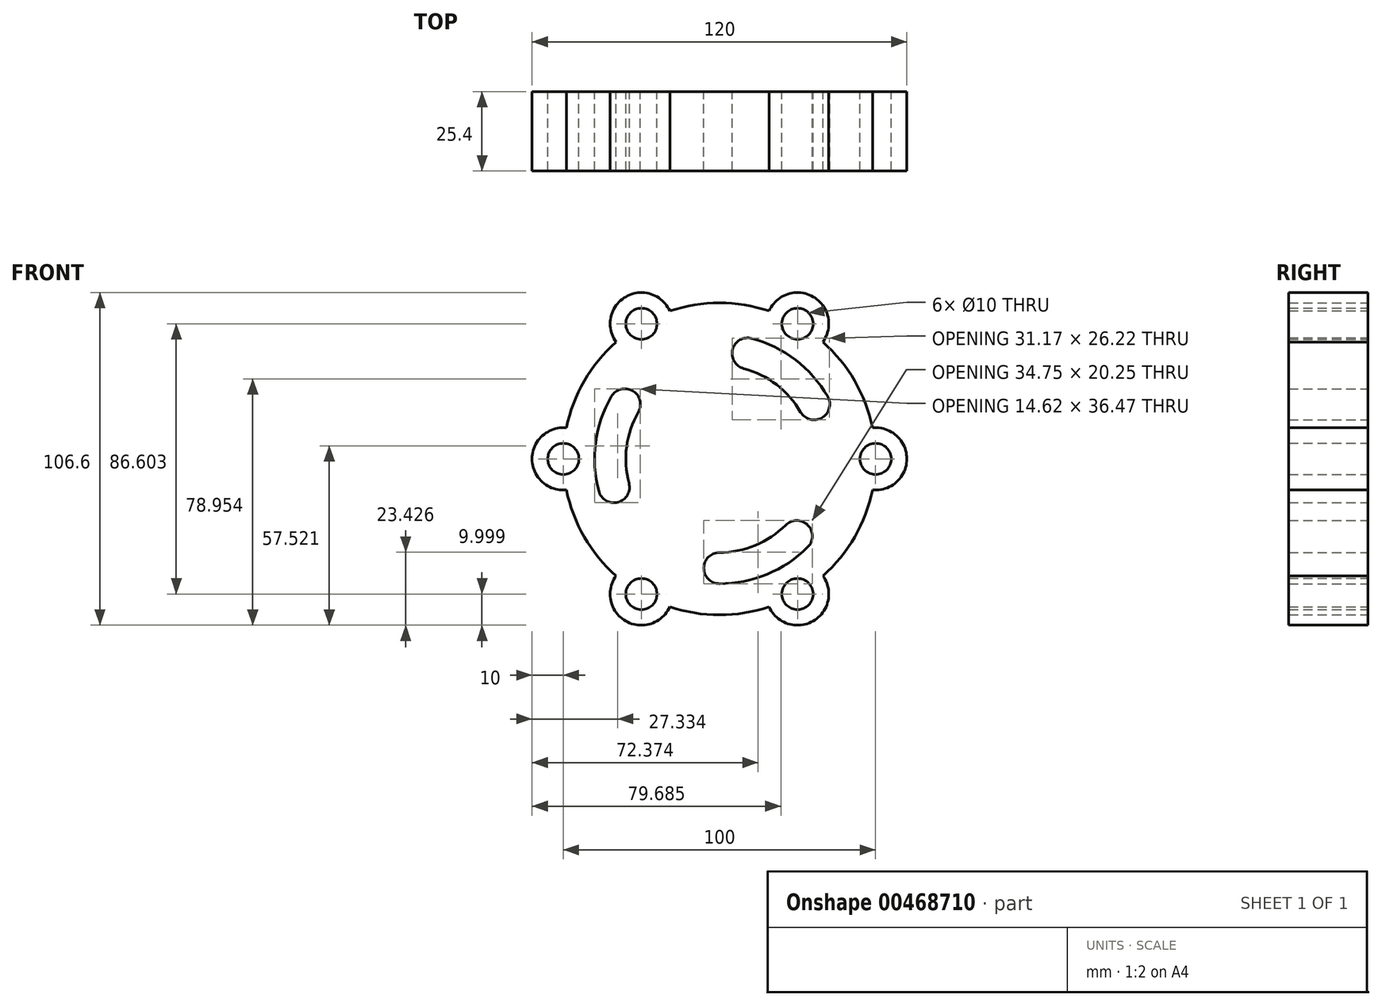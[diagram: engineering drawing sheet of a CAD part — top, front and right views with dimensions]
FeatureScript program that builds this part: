
annotation { "Feature Type Name" : "Feature", "Feature Type Description" : "" }
export const myFeature = defineFeature(function(context is Context, id is Id, definition is map)
    precondition{}
    {
        {
            var Q0;
            Q0=qCreatedBy(makeId("Front.planeOp"),FACE);
            var sketch = newSketch(context, id + "F0", { "sketchPlane" : qUnion([Q0])});
            skArc(sketch, "E0", {"start": v(-49, -9.95) * mm, "mid": v(-43.3, -25) * mm, "end": v(-33.12, -37.46) * mm});
            skArc(sketch, "E1", {"start": v(49, -9.95) * mm, "mid": v(60, 0) * mm, "end": v(49, 9.95) * mm});
            skCircle(sketch, "E2", {"center": v(50, 0) * mm, "radius": 5 * mm});
            skArc(sketch, "E3.1.0", {"start": v(33.12, 37.46) * mm, "mid": v(30, 51.96) * mm, "end": v(15.88, 47.41) * mm});
            skCircle(sketch, "E3.1.1", {"center": v(25, 43.3) * mm, "radius": 5 * mm});
            skArc(sketch, "E3.2.0", {"start": v(-15.88, 47.41) * mm, "mid": v(-30, 51.96) * mm, "end": v(-33.12, 37.46) * mm});
            skCircle(sketch, "E3.2.1", {"center": v(-25, 43.3) * mm, "radius": 5 * mm});
            skArc(sketch, "E3.3.0", {"start": v(-49, 9.95) * mm, "mid": v(-60, 0) * mm, "end": v(-49, -9.95) * mm});
            skCircle(sketch, "E3.3.1", {"center": v(-50, 0) * mm, "radius": 5 * mm});
            skArc(sketch, "E3.4.0", {"start": v(-33.12, -37.46) * mm, "mid": v(-30, -51.96) * mm, "end": v(-15.88, -47.41) * mm});
            skCircle(sketch, "E3.4.1", {"center": v(-25, -43.3) * mm, "radius": 5 * mm});
            skArc(sketch, "E3.5.0", {"start": v(15.88, -47.41) * mm, "mid": v(30, -51.96) * mm, "end": v(33.12, -37.46) * mm});
            skCircle(sketch, "E3.5.1", {"center": v(25, -43.3) * mm, "radius": 5 * mm});
            skArc(sketch, "E4.trimOffspring", {"start": v(-33.12, 37.46) * mm, "mid": v(-43.3, 25) * mm, "end": v(-49, 9.95) * mm});
            skArc(sketch, "E5.trimOffspring", {"start": v(-15.88, -47.41) * mm, "mid": v(0, -50) * mm, "end": v(15.88, -47.41) * mm});
            skArc(sketch, "E6.trimOffspring", {"start": v(33.12, -37.46) * mm, "mid": v(43.3, -25) * mm, "end": v(49, -9.95) * mm});
            skArc(sketch, "E7.trimOffspring", {"start": v(49, 9.95) * mm, "mid": v(43.3, 25) * mm, "end": v(33.12, 37.46) * mm});
            skArc(sketch, "E8.trimOffspring", {"start": v(15.88, 47.41) * mm, "mid": v(0, 50) * mm, "end": v(-15.88, 47.41) * mm});
            skCircle(sketch, "E9", {"center": v(0, 0) * mm, "radius": 35 * mm, "construction": true});
            skLineSegment(sketch, "E10", {"start": v(0, 0) * mm, "end": v(25.98, 15) * mm, "construction": true});
            skLineSegment(sketch, "E11", {"start": v(0, 0) * mm, "end": v(7.76, 28.98) * mm, "construction": true});
            skPoint(sketch, "E12", {"position": v(9.06, 33.8) * mm});
            skPoint(sketch, "E13", {"position": v(30.31, 17.5) * mm});
            skArc(sketch, "E14", {"start": v(10.35, 38.64) * mm, "mid": v(4.23, 35.1) * mm, "end": v(7.76, 28.98) * mm});
            skArc(sketch, "E15", {"start": v(25.98, 15) * mm, "mid": v(32.81, 13.17) * mm, "end": v(34.64, 20) * mm});
            skArc(sketch, "E16", {"start": v(25.98, 15) * mm, "mid": v(18.26, 23.8) * mm, "end": v(7.76, 28.98) * mm});
            skArc(sketch, "E17", {"start": v(34.64, 20) * mm, "mid": v(24.35, 31.73) * mm, "end": v(10.35, 38.64) * mm});
            skArc(sketch, "E18.1.0", {"start": v(-34.64, 20) * mm, "mid": v(-39.66, 5.22) * mm, "end": v(-38.64, -10.35) * mm});
            skArc(sketch, "E18.1.1", {"start": v(-25.98, 15) * mm, "mid": v(-29.74, 3.92) * mm, "end": v(-28.98, -7.76) * mm});
            skArc(sketch, "E18.1.2", {"start": v(-38.64, -10.35) * mm, "mid": v(-32.51, -13.89) * mm, "end": v(-28.98, -7.76) * mm});
            skArc(sketch, "E18.1.3", {"start": v(-25.98, 15) * mm, "mid": v(-27.81, 21.83) * mm, "end": v(-34.64, 20) * mm});
            skArc(sketch, "E18.2.0", {"start": v(0, -40) * mm, "mid": v(15.3, -36.96) * mm, "end": v(28.28, -28.28) * mm});
            skArc(sketch, "E18.2.1", {"start": v(0, -30) * mm, "mid": v(11.48, -27.72) * mm, "end": v(21.21, -21.21) * mm});
            skArc(sketch, "E18.2.2", {"start": v(28.28, -28.28) * mm, "mid": v(28.28, -21.21) * mm, "end": v(21.21, -21.21) * mm});
            skArc(sketch, "E18.2.3", {"start": v(0, -30) * mm, "mid": v(-5, -35) * mm, "end": v(0, -40) * mm});
            skLineSegment(sketch, "E19.trimOffspring", {"start": v(30.31, 17.5) * mm, "end": v(43.3, 25) * mm, "construction": true});
            skLineSegment(sketch, "E20.trimOffspring", {"start": v(10.35, 38.64) * mm, "end": v(12.94, 48.3) * mm, "construction": true});
            skSolve(sketch);
        }
        {
            var Q0;
            Q0=makeQuery(id+"F0.imprint","IMPRINT",FACE,{"disambiguationData":[TD([[makeQuery(id+"F0.imprint","IMPRINT",EDGE,{"derivedFrom":sQuery(id+"F0.wireOp",EDGE,"E0")}),1.0]])]});
            extrude(context, id + "F1", {"entities" : qUnion([Q0]), "endBound" : BoundingType.SYMMETRIC, "depth" : 25.4 * mm});
        }
    });
